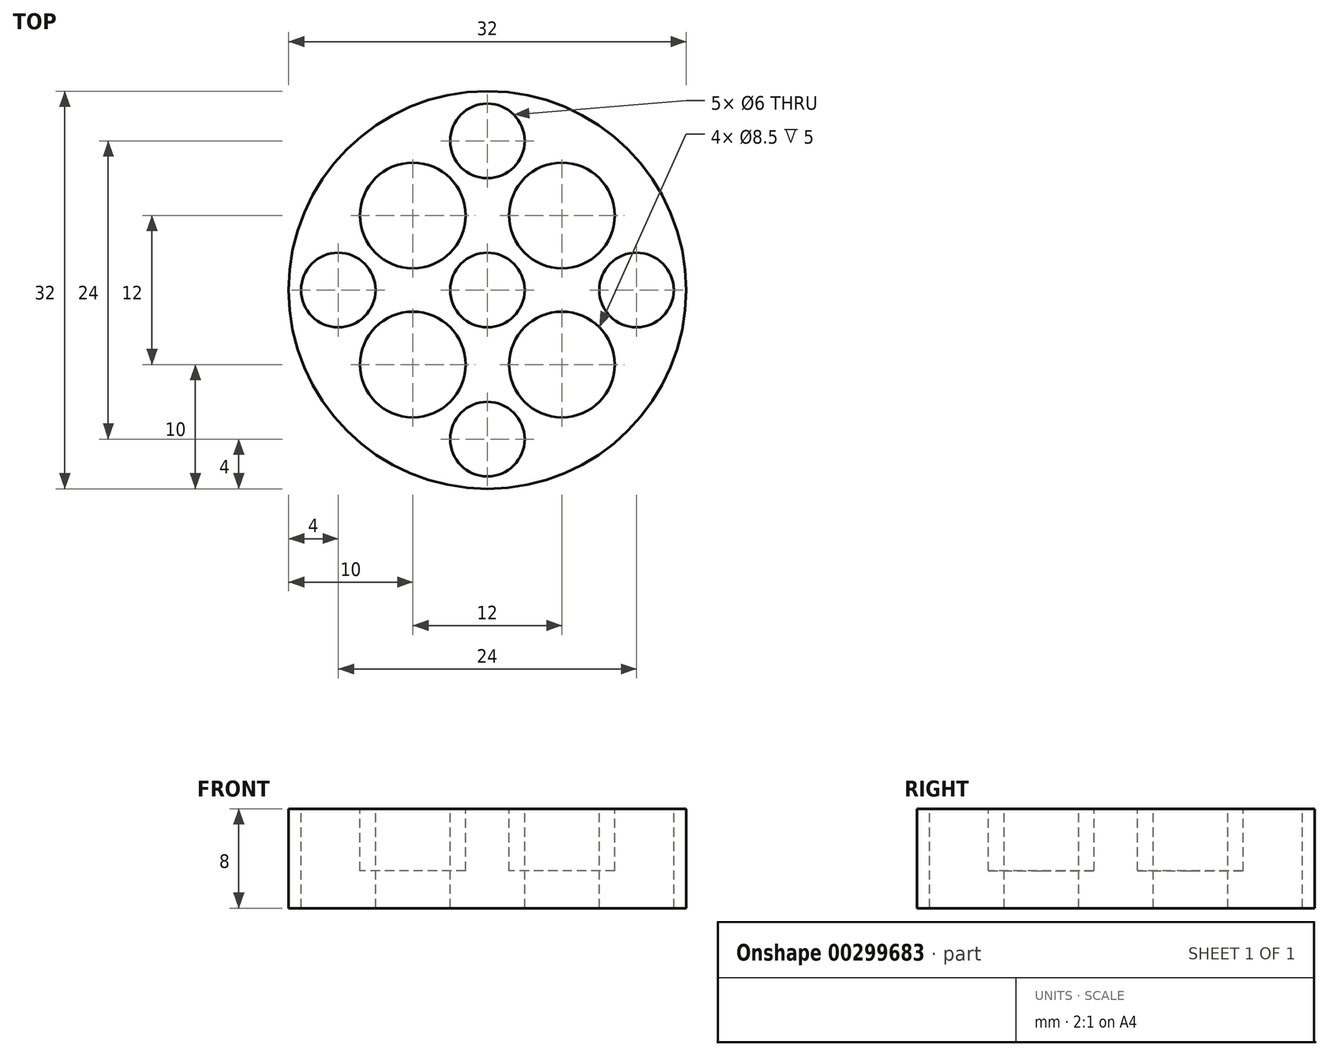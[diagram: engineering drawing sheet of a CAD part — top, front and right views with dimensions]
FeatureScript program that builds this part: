
annotation { "Feature Type Name" : "Feature", "Feature Type Description" : "" }
export const myFeature = defineFeature(function(context is Context, id is Id, definition is map)
    precondition{}
    {
        {
            var Q0;
            Q0=qCreatedBy(makeId("Top.planeOp"),FACE);
            var sketch = newSketch(context, id + "F0", { "sketchPlane" : qUnion([Q0])});
            skCircle(sketch, "E0", {"center": v(0, 0) * mm, "radius": 16 * mm});
            skSolve(sketch);
        }
        {
            var Q0;
            Q0 = qSketchRegion(id + "F0", true);
            extrude(context, id + "F1", {"entities" : qUnion([Q0]), "depth" : 8 * mm});
        }
        {
            var Q0;
            Q0=makeQuery(id+"F1.opExtrude","CAP_FACE",FACE,{"disambiguationData":[OSD([sQuery(id+"F0.wireOp",EDGE,"E0")])],"isStart":false});
            var sketch = newSketch(context, id + "F2", { "sketchPlane" : qUnion([Q0])});
            skLineSegment(sketch, "E1.bottom", {"start": v(6, -6) * mm, "end": v(-6, -6) * mm});
            skLineSegment(sketch, "E1.top", {"start": v(6, 6) * mm, "end": v(-6, 6) * mm});
            skLineSegment(sketch, "E1.left", {"start": v(6, -6) * mm, "end": v(6, 6) * mm});
            skLineSegment(sketch, "E1.right", {"start": v(-6, -6) * mm, "end": v(-6, 6) * mm});
            skPoint(sketch, "E1.middle", {"position": v(0, 0) * mm});
            skCircle(sketch, "E2", {"center": v(-6, 6) * mm, "radius": 4.25 * mm});
            skCircle(sketch, "E3", {"center": v(6, 6) * mm, "radius": 4.25 * mm});
            skCircle(sketch, "E4", {"center": v(6, -6) * mm, "radius": 4.25 * mm});
            skCircle(sketch, "E5", {"center": v(-6, -6) * mm, "radius": 4.25 * mm});
            skSolve(sketch);
        }
        {
            var Q0;
            {var subQ0=sQuery(id+"F2.wireOp",EDGE,"E1.left");var subQ1=sQuery(id+"F2.wireOp",EDGE,"E1.bottom");var subQ2=makeQuery(id+"F2.imprint","INTERSECT",VERTEX,{"derivedFrom":[subQ1,subQ0]});Q0=makeQuery(id+"F2.imprint","IMPRINT",FACE,{"disambiguationData":[TD([[makeQuery(id+"F2.imprint","IMPRINT",EDGE,{"disambiguationData":[TD([[subQ2,-1.0]])],"derivedFrom":subQ1}),-1.0]])]});}
            var Q1;
            {var subQ0=sQuery(id+"F2.wireOp",EDGE,"E1.left");var subQ1=sQuery(id+"F2.wireOp",EDGE,"E1.bottom");var subQ2=makeQuery(id+"F2.imprint","INTERSECT",VERTEX,{"derivedFrom":[subQ1,subQ0]});Q1=makeQuery(id+"F2.imprint","IMPRINT",FACE,{"disambiguationData":[TD([[makeQuery(id+"F2.imprint","IMPRINT",EDGE,{"disambiguationData":[TD([[subQ2,-1.0]])],"derivedFrom":subQ1}),1.0]])]});}
            var Q2;
            {var subQ0=sQuery(id+"F2.wireOp",EDGE,"E1.right");var subQ1=sQuery(id+"F2.wireOp",EDGE,"E1.bottom");var subQ2=makeQuery(id+"F2.imprint","INTERSECT",VERTEX,{"derivedFrom":[subQ1,subQ0]});Q2=makeQuery(id+"F2.imprint","IMPRINT",FACE,{"disambiguationData":[TD([[makeQuery(id+"F2.imprint","IMPRINT",EDGE,{"disambiguationData":[TD([[subQ2,1.0]])],"derivedFrom":subQ1}),-1.0]])]});}
            var Q3;
            {var subQ0=sQuery(id+"F2.wireOp",EDGE,"E1.right");var subQ1=sQuery(id+"F2.wireOp",EDGE,"E1.bottom");var subQ2=makeQuery(id+"F2.imprint","INTERSECT",VERTEX,{"derivedFrom":[subQ1,subQ0]});Q3=makeQuery(id+"F2.imprint","IMPRINT",FACE,{"disambiguationData":[TD([[makeQuery(id+"F2.imprint","IMPRINT",EDGE,{"disambiguationData":[TD([[subQ2,1.0]])],"derivedFrom":subQ1}),1.0]])]});}
            var Q4;
            {var subQ0=sQuery(id+"F2.wireOp",EDGE,"E1.left");var subQ1=sQuery(id+"F2.wireOp",EDGE,"E1.top");var subQ2=makeQuery(id+"F2.imprint","INTERSECT",VERTEX,{"derivedFrom":[subQ1,subQ0]});Q4=makeQuery(id+"F2.imprint","IMPRINT",FACE,{"disambiguationData":[TD([[makeQuery(id+"F2.imprint","IMPRINT",EDGE,{"disambiguationData":[TD([[subQ2,-1.0]])],"derivedFrom":subQ1}),1.0]])]});}
            var Q5;
            {var subQ0=sQuery(id+"F2.wireOp",EDGE,"E1.left");var subQ1=sQuery(id+"F2.wireOp",EDGE,"E1.top");var subQ2=makeQuery(id+"F2.imprint","INTERSECT",VERTEX,{"derivedFrom":[subQ1,subQ0]});Q5=makeQuery(id+"F2.imprint","IMPRINT",FACE,{"disambiguationData":[TD([[makeQuery(id+"F2.imprint","IMPRINT",EDGE,{"disambiguationData":[TD([[subQ2,-1.0]])],"derivedFrom":subQ1}),-1.0]])]});}
            var Q6;
            {var subQ0=sQuery(id+"F2.wireOp",EDGE,"E1.right");var subQ1=sQuery(id+"F2.wireOp",EDGE,"E1.top");var subQ2=makeQuery(id+"F2.imprint","INTERSECT",VERTEX,{"derivedFrom":[subQ1,subQ0]});Q6=makeQuery(id+"F2.imprint","IMPRINT",FACE,{"disambiguationData":[TD([[makeQuery(id+"F2.imprint","IMPRINT",EDGE,{"disambiguationData":[TD([[subQ2,1.0]])],"derivedFrom":subQ1}),-1.0]])]});}
            var Q7;
            {var subQ0=sQuery(id+"F2.wireOp",EDGE,"E1.right");var subQ1=sQuery(id+"F2.wireOp",EDGE,"E1.top");var subQ2=makeQuery(id+"F2.imprint","INTERSECT",VERTEX,{"derivedFrom":[subQ1,subQ0]});Q7=makeQuery(id+"F2.imprint","IMPRINT",FACE,{"disambiguationData":[TD([[makeQuery(id+"F2.imprint","IMPRINT",EDGE,{"disambiguationData":[TD([[subQ2,1.0]])],"derivedFrom":subQ1}),1.0]])]});}
            extrude(context, id + "F3", {"entities" : qUnion([Q0, Q1, Q2, Q3, Q4, Q5, Q6, Q7]), "operationType" : NewBodyOperationType.REMOVE, "oppositeDirection" : true, "depth" : 5 * mm});
        }
        {
            var Q0;
            Q0=makeQuery(id+"F1.opExtrude","CAP_FACE",FACE,{"disambiguationData":[OSD([sQuery(id+"F0.wireOp",EDGE,"E0")])],"isStart":false});
            var sketch = newSketch(context, id + "F4", { "sketchPlane" : qUnion([Q0])});
            skCircle(sketch, "E6", {"center": v(0, 0) * mm, "radius": 3 * mm});
            skCircle(sketch, "E7", {"center": v(-12, 0) * mm, "radius": 3 * mm});
            skCircle(sketch, "E8", {"center": v(0, 12) * mm, "radius": 3 * mm});
            skCircle(sketch, "E9", {"center": v(12, 0) * mm, "radius": 3 * mm});
            skCircle(sketch, "E10", {"center": v(0, -12) * mm, "radius": 3 * mm});
            skSolve(sketch);
        }
        {
            var Q0;
            Q0 = qSketchRegion(id + "F4", true);
            extrude(context, id + "F5", {"entities" : qUnion([Q0]), "operationType" : NewBodyOperationType.REMOVE, "oppositeDirection" : true, "depth" : 25 * mm});
        }
    });
